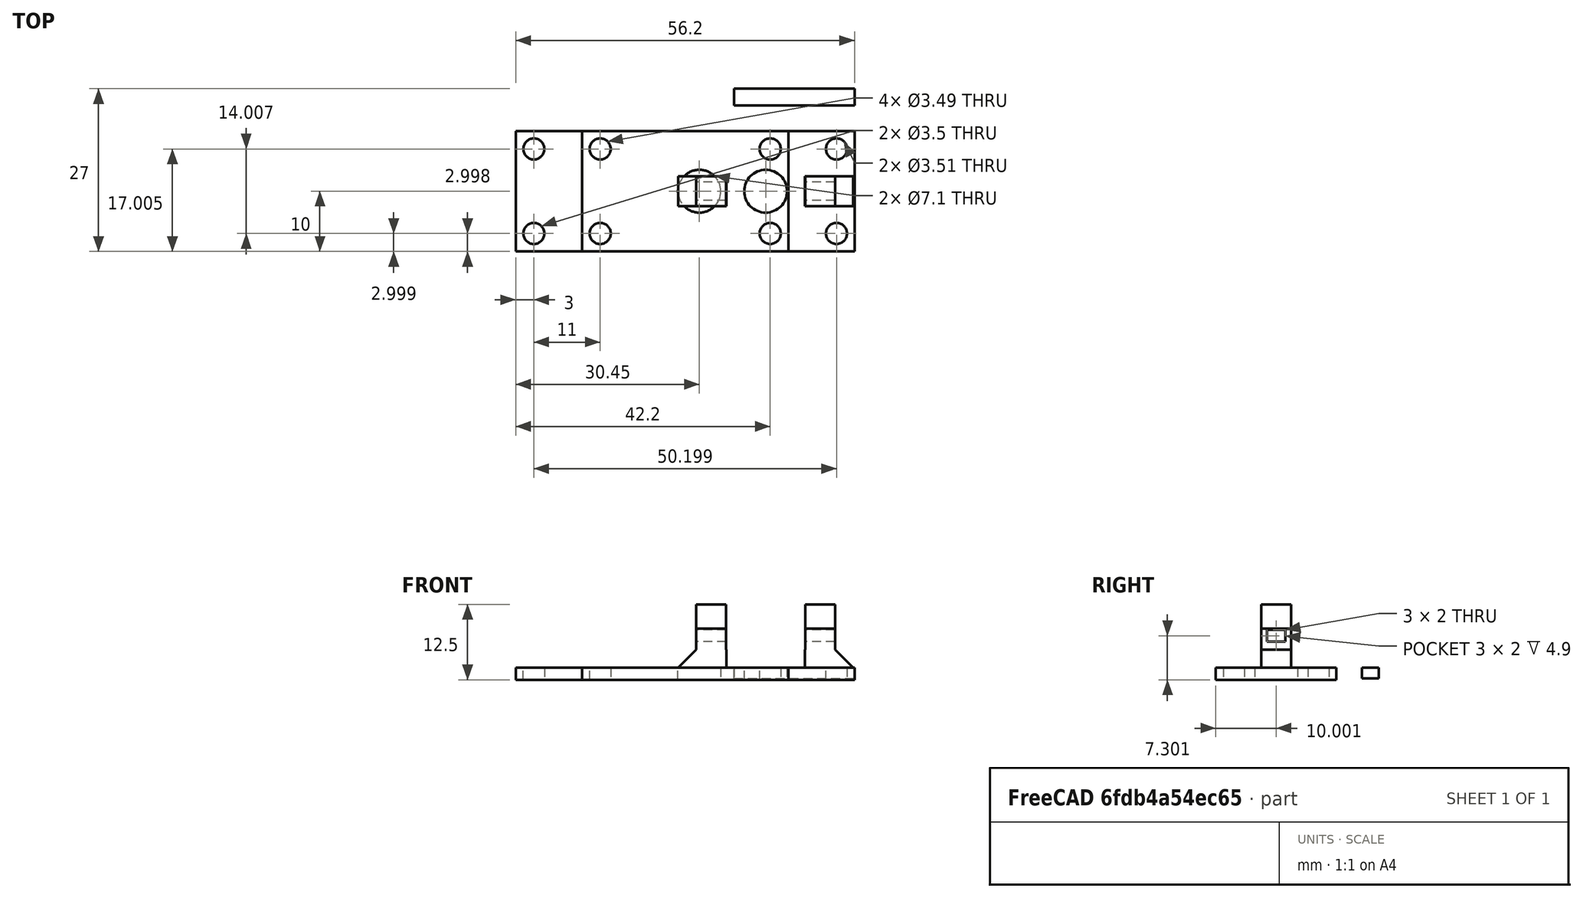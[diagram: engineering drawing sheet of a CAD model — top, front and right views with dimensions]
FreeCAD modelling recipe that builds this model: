
FCSTD DOCUMENT  (FreeCAD 0.17R13522 (Git))
Label: base_inferior_con_soportes_v3
License: CreativeCommons Attribution-ShareAlike
LicenseURL: http://creativecommons.org/licenses/by-sa/4.0/
objects: Part::Extrusion×10, Part::Part2DObjectPython×8, Part::Cut×8, Part::Feature×6, Part::Fuse×6, Part::Box×2, Part::Chamfer×2
note: 42 computed .brp shape members not serialized (recipe doc carries the construction recipe); baked Part::Feature solids carry a one-line shape summary decoded from their .brp

FEATURE [Part::Box] Box  label="placa base"
  AttacherType = Attacher::AttachEngine3D
  Height = 2
  Length = 45.2
  Width = 20
FEATURE [Part::Part2DObjectPython] Circle  label="taladro inferior izquierdo"  # Draft 2D object (typed FeaturePython)
  FirstAngle = 0
  LastAngle = 0
  MakeFace = false
  Placement = pos=(3,2.99873,2) rot=(0,0,1;3.14159rad)
  Radius = 1.74945
FEATURE [Part::Part2DObjectPython] Circle001  label="taladro inferior derecho"  # Draft 2D object (typed FeaturePython)
  FirstAngle = 0
  LastAngle = 0
  MakeFace = false
  Placement = pos=(42.1991,2.99781,2) rot=(0,0,1;3.14159rad)
  Radius = 1.7464
FEATURE [Part::Part2DObjectPython] Circle002  label="taladro superior derecho"  # Draft 2D object (typed FeaturePython)
  FirstAngle = 0
  LastAngle = 0
  MakeFace = false
  Placement = pos=(42.2,17.005,2) rot=(0,0,1;3.14159rad)
  Radius = 1.75369
FEATURE [Part::Part2DObjectPython] Circle003  label="taladro superior izquierdo"  # Draft 2D object (typed FeaturePython)
  FirstAngle = 0
  LastAngle = 0
  MakeFace = false
  Placement = pos=(3,17.005,2) rot=(0,0,1;3.14159rad)
  Radius = 1.74699
FEATURE [Part::Extrusion] Extrude
  Base = -> Circle003
  Dir = (0,0,1)
  DirMode = 2
  FaceMakerClass = Part::FaceMakerBullseye
  LengthFwd = 10
  LengthRev = 0
  Placement = pos=(0,0,-5) rot=(0,0,1;0rad)
  Solid = true
  Symmetric = false
FEATURE [Part::Extrusion] Extrude001
  Base = -> Circle
  Dir = (0,0,1)
  DirMode = 2
  FaceMakerClass = Part::FaceMakerBullseye
  LengthFwd = 10
  LengthRev = 0
  Placement = pos=(0,0,-5) rot=(0,0,1;0rad)
  Solid = true
  Symmetric = false
FEATURE [Part::Extrusion] Extrude002
  Base = -> Circle001
  Dir = (0,0,1)
  DirMode = 2
  FaceMakerClass = Part::FaceMakerBullseye
  LengthFwd = 10
  LengthRev = 0
  Placement = pos=(0,0,-5) rot=(0,0,1;0rad)
  Solid = true
  Symmetric = false
FEATURE [Part::Extrusion] Extrude003
  Base = -> Circle002
  Dir = (0,0,1)
  DirMode = 2
  FaceMakerClass = Part::FaceMakerBullseye
  LengthFwd = 10
  LengthRev = 0
  Placement = pos=(0,0,-5) rot=(0,0,1;0rad)
  Solid = true
  Symmetric = false
FEATURE [Part::Cut] Cut
  Base = -> Box
  Refine = true
  Tool = -> Extrude001
FEATURE [Part::Cut] Cut001
  Base = -> Cut
  Refine = true
  Tool = -> Extrude
FEATURE [Part::Part2DObjectPython] Circle004  # Draft 2D object (typed FeaturePython)
  FirstAngle = 0
  LastAngle = 0
  MakeFace = false
  Placement = pos=(30.45,10,2) rot=(0,0,1;3.14159rad)
  Radius = 3.55
FEATURE [Part::Extrusion] Extrude004
  Base = -> Circle004
  Dir = (0,0,1)
  DirMode = 2
  FaceMakerClass = Part::FaceMakerBullseye
  LengthFwd = 10
  LengthRev = 0
  Placement = pos=(0,0,-4) rot=(0,0,1;0rad)
  Solid = true
  Symmetric = false
FEATURE [Part::Cut] Cut002
  Base = -> Cut001
  Refine = true
  Tool = -> Extrude002
FEATURE [Part::Cut] Cut003  label="base con taladros en esquina"
  Base = -> Cut002
  Refine = true
  Tool = -> Extrude003
FEATURE [Part::Feature] Clone002_solid  label="Clone002 (Solid)"
  Placement = pos=(22.6,40,0) rot=(0,0,1;0rad)
  shape: bbox 6 x 5 x 8 mm, 10 faces (baked)
FEATURE [Part::Feature] Clone001001  label="Clone003"
  Placement = pos=(38.3,10,0) rot=(0,0,1;0rad)
  shape: bbox 6 x 5 x 8 mm, 10 faces (baked)
FEATURE [Part::Feature] Cut004_solid001001  label="base con agujeros (Solid)002"
  shape: bbox 45.2 x 20 x 2 mm, 11 faces (baked)
FEATURE [Part::Fuse] Fusion
  Base = -> Clone002_solid
  Refine = true
  Tool = -> Cut004_solid001001
FEATURE [Part::Chamfer] Chamfer
  Base = -> Fusion
  Edges = 1 edges r=3: [Edge24]
FEATURE [Part::Fuse] Fusion001
  Base = -> Clone001001
  Refine = true
  Tool = -> Chamfer
FEATURE [Part::Chamfer] Chamfer001
  Base = -> Fusion001
  Edges = 1 edges r=3: [Edge24]
FEATURE [Part::Box] Box001  label="Cube"
  AttacherType = Attacher::AttachEngine3D
  Height = 10
  Length = 6
  Placement = pos=(31,6,5) rot=(0,0,1;0rad)
  Width = 15
FEATURE [Part::Feature] Box001001  label="Cube001"
  Placement = pos=(23.9,5,5) rot=(0,0,1;0rad)
  shape: bbox 6 x 15 x 10 mm, 6 faces (baked)
FEATURE [Part::Cut] Cut005
  Base = -> Chamfer001
  Refine = true
  Tool = -> Box001
FEATURE [Part::Cut] Cut006
  Base = -> Cut005
  Refine = true
  Tool = -> Box001001
FEATURE [Part::Part2DObjectPython] Rectangle002  # Draft 2D object (typed FeaturePython)
  ChamferSize = 0
  Columns = 1
  FilletRadius = 0
  Height = 4.95
  Length = 5
  MakeFace = true
  Placement = pos=(18.95,12.5,8.5001) rot=(0,0,-1;1.5708rad)
  Rows = 1
FEATURE [Part::Extrusion] Extrude005
  Base = -> Rectangle002
  Dir = (0,0,1)
  DirMode = 2
  FaceMakerClass = Part::FaceMakerBullseye
  LengthFwd = 4
  LengthRev = 0
  Solid = false
  Symmetric = false
FEATURE [Part::Extrusion] Extrude006
  Base = -> Rectangle002
  Dir = (0,0,1)
  DirMode = 2
  FaceMakerClass = Part::FaceMakerBullseye
  LengthFwd = 4
  LengthRev = 0
  Solid = false
  Symmetric = false
FEATURE [Part::Fuse] Fusion002
  Base = -> Cut006
  Refine = true
  Tool = -> Extrude005
FEATURE [Part::Fuse] Fusion003
  Base = -> Extrude006
  Refine = true
  Tool = -> Fusion002
FEATURE [Part::Part2DObjectPython] Rectangle003  # Draft 2D object (typed FeaturePython)
  ChamferSize = 0
  Columns = 1
  FilletRadius = 0
  Height = 4.95
  Length = 5
  MakeFace = true
  Placement = pos=(37,12.5,8.5001) rot=(0,0,-1;1.5708rad)
  Rows = 1
FEATURE [Part::Extrusion] Extrude007
  Base = -> Rectangle003
  Dir = (0,0,1)
  DirMode = 2
  FaceMakerClass = Part::FaceMakerBullseye
  LengthFwd = 4
  LengthRev = 0
  Solid = false
  Symmetric = false
FEATURE [Part::Extrusion] Extrude008
  Base = -> Rectangle003
  Dir = (0,0,1)
  DirMode = 2
  FaceMakerClass = Part::FaceMakerBullseye
  LengthFwd = 4
  LengthRev = 0
  Solid = false
  Symmetric = false
FEATURE [Part::Fuse] Fusion004
  Base = -> Fusion003
  Refine = true
  Tool = -> Extrude008
FEATURE [Part::Fuse] Fusion005
  Base = -> Extrude007
  Placement = pos=(3,0,0) rot=(0,0,1;0rad)
  Refine = true
  Tool = -> Fusion004
FEATURE [Part::Feature] Extrude009001  label="Extrude010"
  Placement = pos=(3,0,0) rot=(0,0,1;0rad)
  shape: bbox 36 x 3 x 2 mm, 6 faces (baked)
FEATURE [Part::Cut] Cut007
  Base = -> Fusion005
  Placement = pos=(8,0,0) rot=(0,0,1;0rad)
  Refine = true
  Tool = -> Extrude009001
FEATURE [Part::Part2DObjectPython] Rectangle  # Draft 2D object (typed FeaturePython)
  ChamferSize = 0
  Columns = 1
  FilletRadius = 0
  Height = 1.8
  Length = 2.8
  MakeFace = true
  Placement = pos=(56.2,27.001,2.00104) rot=(0.57735,-0.57735,0.57735;4.18879rad)
  Rows = 1
FEATURE [Part::Extrusion] Extrude009001002  label="chaveta1"
  Base = -> Rectangle
  Dir = (1,0,0)
  DirMode = 2
  FaceMakerClass = Part::FaceMakerBullseye
  LengthFwd = 20
  LengthRev = 0
  Placement = pos=(-20,0,0) rot=(0,0,1;0rad)
  Solid = false
  Symmetric = false
FEATURE [Part::Cut] Cut004  label="base con agujeros"
  Base = -> Cut003
  Refine = true
  Tool = -> Extrude004
FEATURE [Part::Feature] Extrude009001002001  label="chaveta002"
  Placement = pos=(-20,0,0) rot=(0,0,1;0rad)
  shape: bbox 20 x 2.8 x 1.8 mm, 6 faces (baked)
